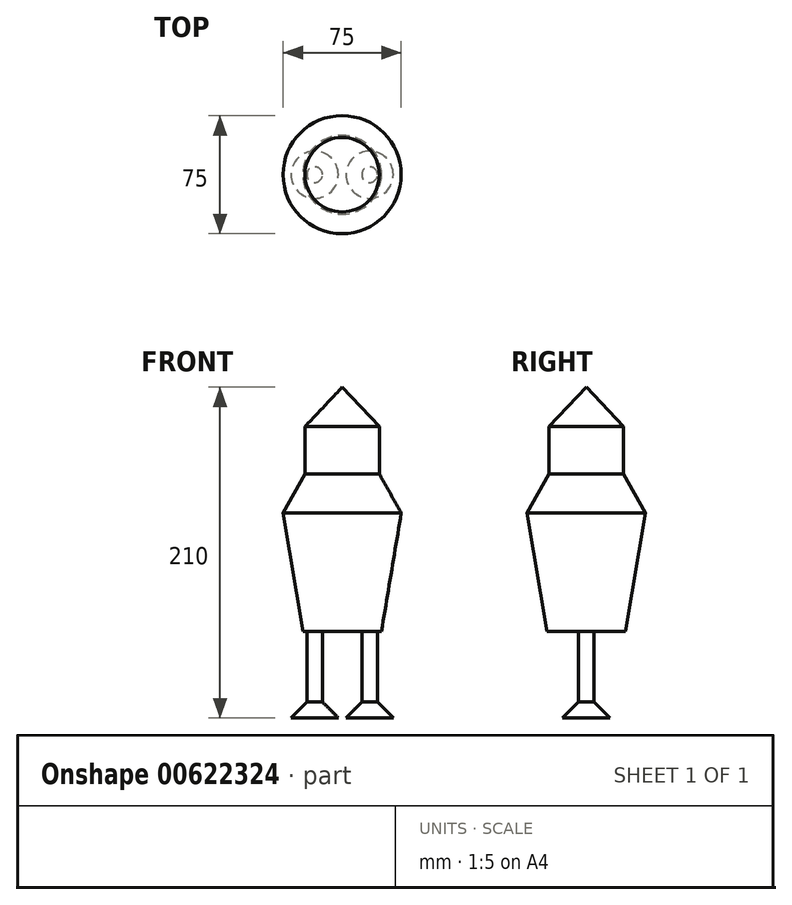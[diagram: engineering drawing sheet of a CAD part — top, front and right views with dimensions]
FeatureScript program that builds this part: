
annotation { "Feature Type Name" : "Feature", "Feature Type Description" : "" }
export const myFeature = defineFeature(function(context is Context, id is Id, definition is map)
    precondition{}
    {
        {
            var Q0;
            Q0=qCreatedBy(makeId("Top.planeOp"),FACE);
            var sketch = newSketch(context, id + "F0", { "sketchPlane" : qUnion([Q0])});
            skCircle(sketch, "E0", {"center": v(-17.46, 0) * mm, "radius": 15 * mm});
            skLineSegment(sketch, "E1", {"start": v(0, 184.29) * mm, "end": v(0, -169.04) * mm, "construction": true});
            skSolve(sketch);
        }
        {
            var Q0;
            Q0=qCreatedBy(makeId("Top.planeOp"),FACE);
            cPlane(context, id + "F1", {"entities" : qUnion([Q0]), "cplaneType" : CPlaneType.OFFSET, "offset" : 10 * mm, "width" : 150 * mm, "height" : 150 * mm});
        }
        {
            var Q0;
            Q0=qCreatedBy(id+"F1.planeOp",FACE);
            var sketch = newSketch(context, id + "F2", { "sketchPlane" : qUnion([Q0])});
            skPoint(sketch, "E2.0", {"position": v(-17.46, 0) * mm});
            skCircle(sketch, "E3", {"center": v(-17.46, 0) * mm, "radius": 5 * mm});
            skSolve(sketch);
        }
        {
            var Q0;
            Q0=makeQuery(id+"F0.imprint","IMPRINT",FACE,{"disambiguationData":[TD([[makeQuery(id+"F0.imprint","IMPRINT",EDGE,{"derivedFrom":sQuery(id+"F0.wireOp",EDGE,"E0")}),1.0]])]});
            var Q1;
            Q1=makeQuery(id+"F2.imprint","IMPRINT",FACE,{"disambiguationData":[TD([[makeQuery(id+"F2.imprint","IMPRINT",EDGE,{"derivedFrom":sQuery(id+"F2.wireOp",EDGE,"E3")}),1.0]])]});
            loft(context, id + "F3", {"sheetProfilesArray" : [{ "sheetProfileEntities" : qUnion([Q0]) }, { "sheetProfileEntities" : qUnion([Q1]) }]});
        }
        {
            var Q0;
            Q0=makeQuery(id+"F3.opLoft","CAP_FACE",FACE,{"disambiguationData":[OSD([makeQuery(id+"F2.imprint","IMPRINT",FACE,{"disambiguationData":[TD([[makeQuery(id+"F2.imprint","IMPRINT",EDGE,{"derivedFrom":sQuery(id+"F2.wireOp",EDGE,"E3")}),1.0]])]})])],"isStart":true});
            extrude(context, id + "F4", {"entities" : qUnion([Q0]), "operationType" : NewBodyOperationType.ADD, "depth" : 45 * mm, "offsetDistance" : 25 * mm});
        }
        {
            var Q0;
            Q0=makeQuery(id+"F3.opLoft","SWEPT_BODY",BODY,{"disambiguationData":[OSD([makeQuery(id+"F0.imprint","IMPRINT",FACE,{"disambiguationData":[TD([[makeQuery(id+"F0.imprint","IMPRINT",EDGE,{"derivedFrom":sQuery(id+"F0.wireOp",EDGE,"E0")}),1.0]])]}),makeQuery(id+"F2.imprint","IMPRINT",FACE,{"disambiguationData":[TD([[makeQuery(id+"F2.imprint","IMPRINT",EDGE,{"derivedFrom":sQuery(id+"F2.wireOp",EDGE,"E3")}),1.0]])]})])]});
            var Q1;
            Q1=qCreatedBy(makeId("Right.planeOp"),FACE);
            mirror(context, id + "F5", {"entities" : qUnion([Q0]), "mirrorPlane" : qUnion([Q1])});
        }
        {
            var Q0;
            Q0=makeQuery(id+"F4.opExtrude","CAP_FACE",FACE,{"disambiguationData":[OSD([makeQuery(id+"F2.imprint","IMPRINT",FACE,{"disambiguationData":[TD([[makeQuery(id+"F2.imprint","IMPRINT",EDGE,{"derivedFrom":sQuery(id+"F2.wireOp",EDGE,"E3")}),1.0]])]})])],"isStart":false});
            cPlane(context, id + "F6", {"entities" : qUnion([Q0]), "cplaneType" : CPlaneType.OFFSET, "offset" : 0 * mm, "width" : 150 * mm, "height" : 150 * mm});
        }
        {
            var Q0;
            Q0=qCreatedBy(id+"F6.planeOp",FACE);
            var sketch = newSketch(context, id + "F7", { "sketchPlane" : qUnion([Q0])});
            skCircle(sketch, "E4", {"center": v(0, 0) * mm, "radius": 25 * mm});
            skSolve(sketch);
        }
        {
            var Q0;
            Q0=makeQuery(id+"F7.imprint","IMPRINT",FACE,{"disambiguationData":[TD([[makeQuery(id+"F7.imprint","IMPRINT",EDGE,{"derivedFrom":sQuery(id+"F7.wireOp",EDGE,"E4")}),1.0]])]});
            cPlane(context, id + "F8", {"entities" : qUnion([Q0]), "cplaneType" : CPlaneType.OFFSET, "offset" : 75 * mm, "width" : 150 * mm, "height" : 150 * mm});
        }
        {
            var Q0;
            Q0=qCreatedBy(id+"F8.planeOp",FACE);
            var sketch = newSketch(context, id + "F9", { "sketchPlane" : qUnion([Q0])});
            skCircle(sketch, "E5", {"center": v(0, 0) * mm, "radius": 37.5 * mm});
            skSolve(sketch);
        }
        {
            var Q0;
            Q0=makeQuery(id+"F7.imprint","IMPRINT",FACE,{"disambiguationData":[TD([[makeQuery(id+"F7.imprint","IMPRINT",EDGE,{"derivedFrom":sQuery(id+"F7.wireOp",EDGE,"E4")}),1.0]])]});
            var Q1;
            Q1=makeQuery(id+"F9.imprint","IMPRINT",FACE,{"disambiguationData":[TD([[makeQuery(id+"F9.imprint","IMPRINT",EDGE,{"derivedFrom":sQuery(id+"F9.wireOp",EDGE,"E5")}),1.0]])]});
            loft(context, id + "F10", {"sheetProfilesArray" : [{ "sheetProfileEntities" : qUnion([Q0]) }, { "sheetProfileEntities" : qUnion([Q1]) }]});
        }
        {
            var Q0;
            Q0=makeQuery(id+"F10.opLoft","CAP_FACE",FACE,{"disambiguationData":[OSD([makeQuery(id+"F9.imprint","IMPRINT",FACE,{"disambiguationData":[TD([[makeQuery(id+"F9.imprint","IMPRINT",EDGE,{"derivedFrom":sQuery(id+"F9.wireOp",EDGE,"E5")}),1.0]])]})])],"isStart":true});
            cPlane(context, id + "F11", {"entities" : qUnion([Q0]), "cplaneType" : CPlaneType.OFFSET, "offset" : 25 * mm, "width" : 150 * mm, "height" : 150 * mm});
        }
        {
            var Q0;
            Q0=qCreatedBy(id+"F11.planeOp",FACE);
            var sketch = newSketch(context, id + "F12", { "sketchPlane" : qUnion([Q0])});
            skCircle(sketch, "E6", {"center": v(0, 0) * mm, "radius": 23.6 * mm});
            skSolve(sketch);
        }
        {
            var Q1;
            Q1=makeQuery(id+"F10.opLoft","CAP_FACE",FACE,{"disambiguationData":[OSD([makeQuery(id+"F9.imprint","IMPRINT",FACE,{"disambiguationData":[TD([[makeQuery(id+"F9.imprint","IMPRINT",EDGE,{"derivedFrom":sQuery(id+"F9.wireOp",EDGE,"E5")}),1.0]])]})])],"isStart":true});
            var Q2;
            Q2=makeQuery(id+"F12.imprint","IMPRINT",FACE,{"disambiguationData":[TD([[makeQuery(id+"F12.imprint","IMPRINT",EDGE,{"derivedFrom":sQuery(id+"F12.wireOp",EDGE,"E6")}),1.0]])]});
            loft(context, id + "F13", {"operationType" : NewBodyOperationType.ADD, "sheetProfilesArray" : [{ "sheetProfileEntities" : qUnion([Q1]) }, { "sheetProfileEntities" : qUnion([Q2]) }]});
        }
        {
            var Q0;
            Q0=makeQuery(id+"F13.opLoft","CAP_FACE",FACE,{"disambiguationData":[OSD([makeQuery(id+"F12.imprint","IMPRINT",FACE,{"disambiguationData":[TD([[makeQuery(id+"F12.imprint","IMPRINT",EDGE,{"derivedFrom":sQuery(id+"F12.wireOp",EDGE,"E6")}),1.0]])]})])],"isStart":true});
            extrude(context, id + "F14", {"entities" : qUnion([Q0]), "operationType" : NewBodyOperationType.ADD, "depth" : 30 * mm, "offsetDistance" : 25 * mm});
        }
        {
            var Q0;
            Q0=makeQuery(id+"F14.opExtrude","CAP_FACE",FACE,{"disambiguationData":[OSD([makeQuery(id+"F12.imprint","IMPRINT",FACE,{"disambiguationData":[TD([[makeQuery(id+"F12.imprint","IMPRINT",EDGE,{"derivedFrom":sQuery(id+"F12.wireOp",EDGE,"E6")}),1.0]])]})])],"isStart":false});
            cPlane(context, id + "F15", {"entities" : qUnion([Q0]), "cplaneType" : CPlaneType.OFFSET, "offset" : 25 * mm, "width" : 150 * mm, "height" : 150 * mm});
        }
        {
            var Q0;
            Q0=qCreatedBy(id+"F15.planeOp",FACE);
            var sketch = newSketch(context, id + "F16", { "sketchPlane" : qUnion([Q0])});
            skPoint(sketch, "E7", {"position": v(0, 0) * mm});
            skSolve(sketch);
        }
        {
            var Q1;
            Q1=makeQuery(id+"F14.opExtrude","CAP_FACE",FACE,{"disambiguationData":[OSD([makeQuery(id+"F12.imprint","IMPRINT",FACE,{"disambiguationData":[TD([[makeQuery(id+"F12.imprint","IMPRINT",EDGE,{"derivedFrom":sQuery(id+"F12.wireOp",EDGE,"E6")}),1.0]])]})])],"isStart":false});
            var Q2;
            Q2=sQuery(id+"F16.wireOp",VERTEX,"E7");
            loft(context, id + "F17", {"operationType" : NewBodyOperationType.ADD, "sheetProfilesArray" : [{ "sheetProfileEntities" : qUnion([Q1]) }, { "sheetProfileEntities" : qUnion([Q2]) }]});
        }
    });
